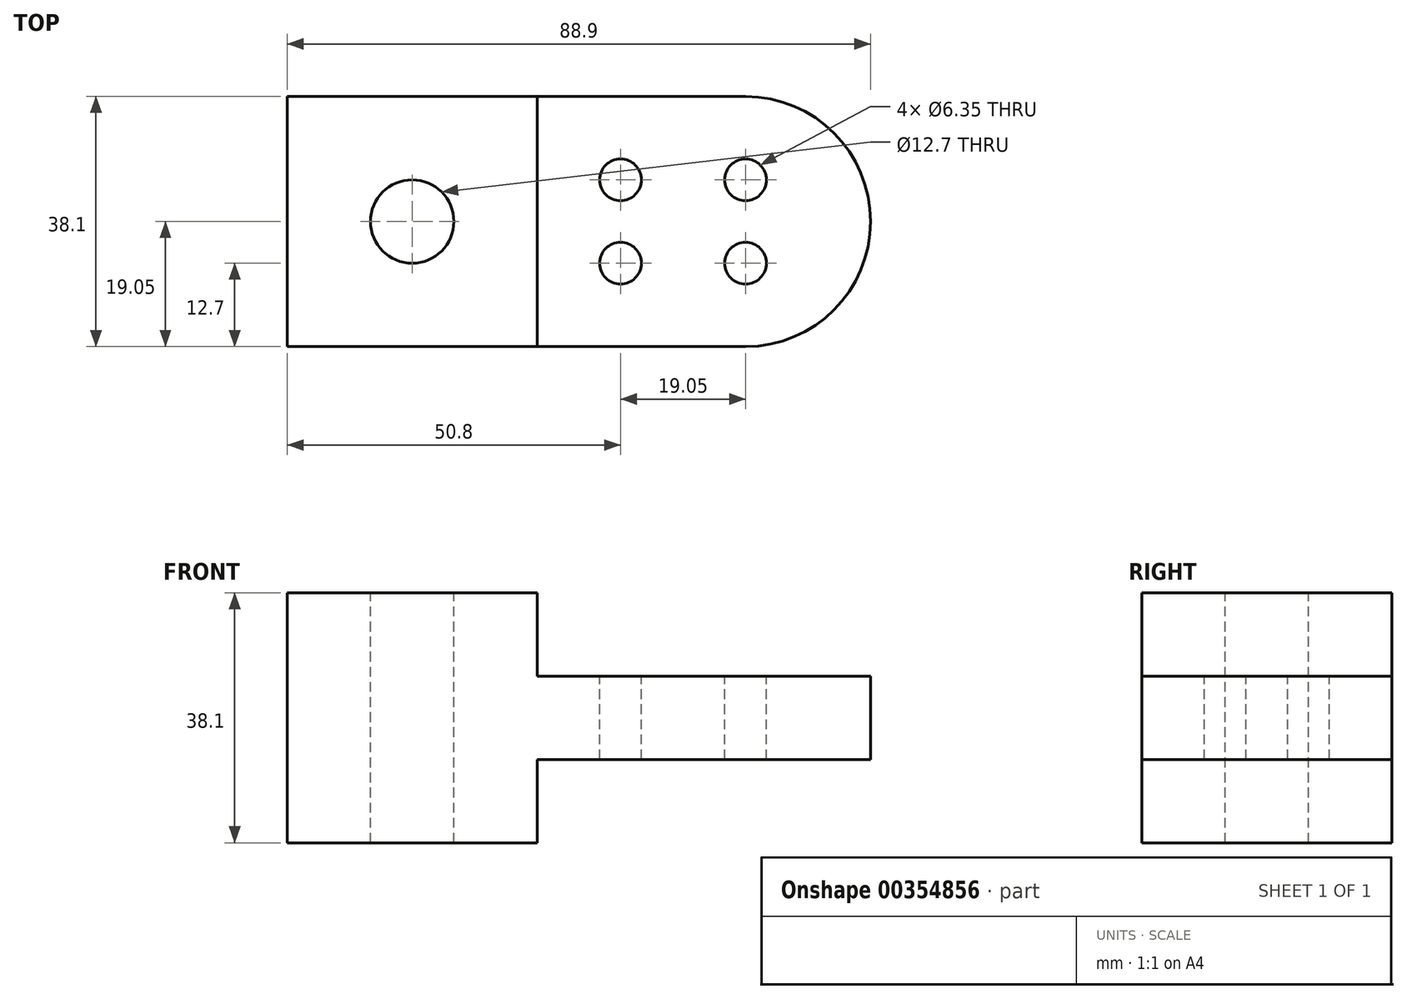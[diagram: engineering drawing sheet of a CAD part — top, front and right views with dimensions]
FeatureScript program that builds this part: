
annotation { "Feature Type Name" : "Feature", "Feature Type Description" : "" }
export const myFeature = defineFeature(function(context is Context, id is Id, definition is map)
    precondition{}
    {
        {
            var Q0;
            Q0=qCreatedBy(makeId("Top.planeOp"),FACE);
            var sketch = newSketch(context, id + "F0", { "sketchPlane" : qUnion([Q0])});
            skLineSegment(sketch, "E0", {"start": v(0, 19.05) * mm, "end": v(-38.1, 19.05) * mm});
            skLineSegment(sketch, "E1", {"start": v(-38.1, 19.05) * mm, "end": v(-38.1, -19.05) * mm});
            skLineSegment(sketch, "E2", {"start": v(-38.1, -19.05) * mm, "end": v(0, -19.05) * mm});
            skLineSegment(sketch, "E3", {"start": v(0, -19.05) * mm, "end": v(0, -6.35) * mm});
            skLineSegment(sketch, "E4", {"start": v(0, 19.05) * mm, "end": v(0, -6.35) * mm});
            skLineSegment(sketch, "E5", {"start": v(0, 19.05) * mm, "end": v(31.75, 19.05) * mm});
            skLineSegment(sketch, "E6", {"start": v(31.75, 19.05) * mm, "end": v(31.75, -19.05) * mm});
            skLineSegment(sketch, "E7", {"start": v(31.75, -19.05) * mm, "end": v(0, -19.05) * mm});
            skArc(sketch, "E8", {"start": v(31.75, -19.05) * mm, "mid": v(50.8, 0) * mm, "end": v(31.75, 19.05) * mm});
            skSolve(sketch);
        }
        {
            var Q0;
            Q0=makeQuery(id+"F0.imprint","IMPRINT",FACE,{"disambiguationData":[TD([[makeQuery(id+"F0.imprint","IMPRINT",EDGE,{"derivedFrom":sQuery(id+"F0.wireOp",EDGE,"E0")}),1.0]])]});
            extrude(context, id + "F1", {"entities" : qUnion([Q0]), "endBound" : BoundingType.SYMMETRIC, "depth" : 38.1 * mm});
        }
        {
            var Q0;
            Q0=makeQuery(id+"F0.imprint","IMPRINT",FACE,{"disambiguationData":[TD([[makeQuery(id+"F0.imprint","IMPRINT",EDGE,{"derivedFrom":sQuery(id+"F0.wireOp",EDGE,"E3")}),-1.0]])]});
            extrude(context, id + "F2", {"entities" : qUnion([Q0]), "operationType" : NewBodyOperationType.ADD, "endBound" : BoundingType.SYMMETRIC, "depth" : 12.7 * mm});
        }
        {
            var Q0;
            Q0=makeQuery(id+"F0.imprint","IMPRINT",FACE,{"disambiguationData":[TD([[makeQuery(id+"F0.imprint","IMPRINT",EDGE,{"derivedFrom":sQuery(id+"F0.wireOp",EDGE,"E6")}),1.0]])]});
            extrude(context, id + "F3", {"entities" : qUnion([Q0]), "operationType" : NewBodyOperationType.ADD, "endBound" : BoundingType.SYMMETRIC, "depth" : 12.7 * mm});
        }
        {
            var Q0;
            Q0=makeQuery(id+"F1.opExtrude","CAP_FACE",FACE,{"disambiguationData":[OSD([sQuery(id+"F0.wireOp",EDGE,"E0"),sQuery(id+"F0.wireOp",EDGE,"E1"),sQuery(id+"F0.wireOp",EDGE,"E2"),sQuery(id+"F0.wireOp",EDGE,"E3"),sQuery(id+"F0.wireOp",EDGE,"E4")])],"isStart":false});
            var sketch = newSketch(context, id + "F4", { "sketchPlane" : qUnion([Q0])});
            skCircle(sketch, "E9", {"center": v(-19.05, 0) * mm, "radius": 6.35 * mm});
            skPoint(sketch, "E9.centerSnap0", {"position": v(-19.05, 19.05) * mm});
            skPoint(sketch, "E9.centerSnap1", {"position": v(-38.1, 0) * mm});
            skSolve(sketch);
        }
        {
            var Q0;
            {var subQ0=sQuery(id+"F0.wireOp",EDGE,"E6");Q0=makeQuery(id+"F3.boolean.opBoolean","MERGE",FACE,{"derivedFrom":[makeQuery(id+"F2.opExtrude","CAP_FACE",FACE,{"disambiguationData":[OSD([sQuery(id+"F0.wireOp",EDGE,"E3"),sQuery(id+"F0.wireOp",EDGE,"E4"),sQuery(id+"F0.wireOp",EDGE,"E5"),subQ0,sQuery(id+"F0.wireOp",EDGE,"E7")])],"isStart":false}),makeQuery(id+"F3.opExtrude","CAP_FACE",FACE,{"disambiguationData":[OSD([subQ0,sQuery(id+"F0.wireOp",EDGE,"E8")])],"isStart":false})]});}
            var sketch = newSketch(context, id + "F5", { "sketchPlane" : qUnion([Q0])});
            skCircle(sketch, "E10", {"center": v(12.7, -6.35) * mm, "radius": 3.18 * mm});
            skCircle(sketch, "E11", {"center": v(12.7, 6.35) * mm, "radius": 3.18 * mm});
            skCircle(sketch, "E12", {"center": v(31.75, 6.35) * mm, "radius": 3.18 * mm});
            skCircle(sketch, "E13", {"center": v(31.75, -6.35) * mm, "radius": 3.18 * mm});
            skSolve(sketch);
        }
        {
            var Q0;
            Q0 = qSketchRegion(id + "F5", true);
            extrude(context, id + "F6", {"entities" : qUnion([Q0]), "operationType" : NewBodyOperationType.REMOVE, "oppositeDirection" : true, "depth" : 25.4 * mm});
        }
        {
            var Q0;
            Q0 = qSketchRegion(id + "F4", true);
            extrude(context, id + "F7", {"entities" : qUnion([Q0]), "operationType" : NewBodyOperationType.REMOVE, "endBound" : BoundingType.THROUGH_ALL, "oppositeDirection" : true, "depth" : 25.4 * mm});
        }
    });
